# Revit family: Shinhoo_MASTER_S
name_source: partatom
category: Оборудование
units: mm (PartAtom-declared; Revit-internal decimal feet)

## family parameters
Всегда вертикально = Нет
Классификация = Нет
На основе рабочей плоскости = Нет
Общий = Нет
При загрузке вырезать с полостями = Нет
Размер круглого соединителя = Использовать диаметр
Тип детали = Вставляется
Точка расчета площади = Нет

## types (7) — shared parameters
ADSK_URL страницы изделия = https://shinhoopump.ru
ADSK_Версия Revit = 2019
ADSK_Версия семейства = 1.0
ADSK_Единица измерения = шт
ADSK_Завод-изготовитель = Shinhoo
ADSK_Количество = 1
ADSK_Коэффициент мощности = 1
ADSK_Материал = Чугун с катафорезным покрытием
ADSK_Напряжение = 230 В
ADSK_Обозначение = ГОСТ 31839-2012, ГОСТ 12.2.007.0-75, ГОСТ 12.2.003-91, ГОСТ Р МЭК 60204-1-2007,  ГОСТ 30804
B = 90 мм
B1 = 45 мм
B2 = 45 мм
H = 128 мм
H1 = 38 мм
H2 = 90 мм
URL = https://shinhoopump.ru
b1_20 = 39 мм
d1 = 27 мм
d6 = 40 мм
r1 = 13 мм
r1_1 = 14 мм
r1_3 = 20 мм
r6 = 20 мм
Изготовитель = Shinhoo
Класс защиты (IP) = IP44
Разработчик = ООО ПРОРУБИМ
Разработчик (телефон) = +7(495)649-85-43
Скорость вращения = 2850
Степень защиты от удара (IK) = IK04
Тип Насоса = Энергоэффективный циркуляционный насос с «мокрым» ротором
Тип основания = встроенный

## per-type parameters (varying)
| type | ADSK_Код изделия | ADSK_Масса | ADSK_Масса_Текст | ADSK_Наименование | ADSK_Наименование краткое | ADSK_Номинальная мощность | ADSK_Полная мощность | ADSK_Расход жидкости | ADSK_Ток | DN | L | Группа модели |
| MASTER S 25-6 130 1x230В - 71111001 | 71111001 | 1.8 | 1.8 | Энергоэффективный циркуляционный насос с «мокрым» ротором MASTER S 25-6 130 1x230В | MASTER S 25-6 130 1x230В | 39 Вт | 39 В·А | 0.000889 м³/с | 0 А | 25 мм | 130 мм | MASTER S 25-6 130 1x230В |
| MASTER S 25-4 180 1x230В - 71111002 | 71111002 | 1.9 | 1.9 | Энергоэффективный циркуляционный насос с «мокрым» ротором MASTER S 25-4 180 1x230В | MASTER S 25-4 180 1x230В | 26 Вт | 26 В·А | 0.000778 м³/с | 0 А | 25 мм | 180 мм | MASTER S 25-4 180 1x230В |
| MASTER S 25-6 180 1x230В - 71111003 | 71111003 | 1.9 | 1.9 | Энергоэффективный циркуляционный насос с «мокрым» ротором MASTER S 25-6 180 1x230В | MASTER S 25-6 180 1x230В | 39 Вт | 39 В·А | 0.000889 м³/с | 0 А | 25 мм | 180 мм | MASTER S 25-6 180 1x230В |
| MASTER S 25-7.5 180 1x230В - 71111004 | 71111004 | 1.9 | 1.9 | Энергоэффективный циркуляционный насос с «мокрым» ротором MASTER S 25-7.5 180 1x230В | MASTER S 25-7.5 180 1x230В | 60 Вт | 60 В·А | 0.001111 м³/с | 1 А | 25 мм | 180 мм | MASTER S 25-7.5 180 1x230В |
| MASTER S 32-4 180 1x230В - 71111005 | 71111005 | 2 | 2 | Энергоэффективный циркуляционный насос с «мокрым» ротором MASTER S 32-4 180 1x230В | MASTER S 32-4 180 1x230В | 26 Вт | 26 В·А | 0.000778 м³/с | 0 А | 32 мм | 180 мм | MASTER S 32-4 180 1x230В |
| MASTER S 32-6 180 1x230В - 71111006 | 71111006 | 2 | 2 | Энергоэффективный циркуляционный насос с «мокрым» ротором MASTER S 32-6 180 1x230В | MASTER S 32-6 180 1x230В | 39 Вт | 39 В·А | 0.000889 м³/с | 0 А | 32 мм | 180 мм | MASTER S 32-6 180 1x230В |
| MASTER S 32-7.5 180 1x230В - 71111007 | 71111007 | 2 | 2 | Энергоэффективный циркуляционный насос с «мокрым» ротором MASTER S 32-7.5 180 1x230В | MASTER S 32-7.5 180 1x230В | 60 Вт | 60 В·А | 0.001111 м³/с | 1 А | 32 мм | 180 мм | MASTER S 32-7.5 180 1x230В |

## geometry (parser evidence)
native form markers: Sweep x2
no freeform markers — native parametric forms only
